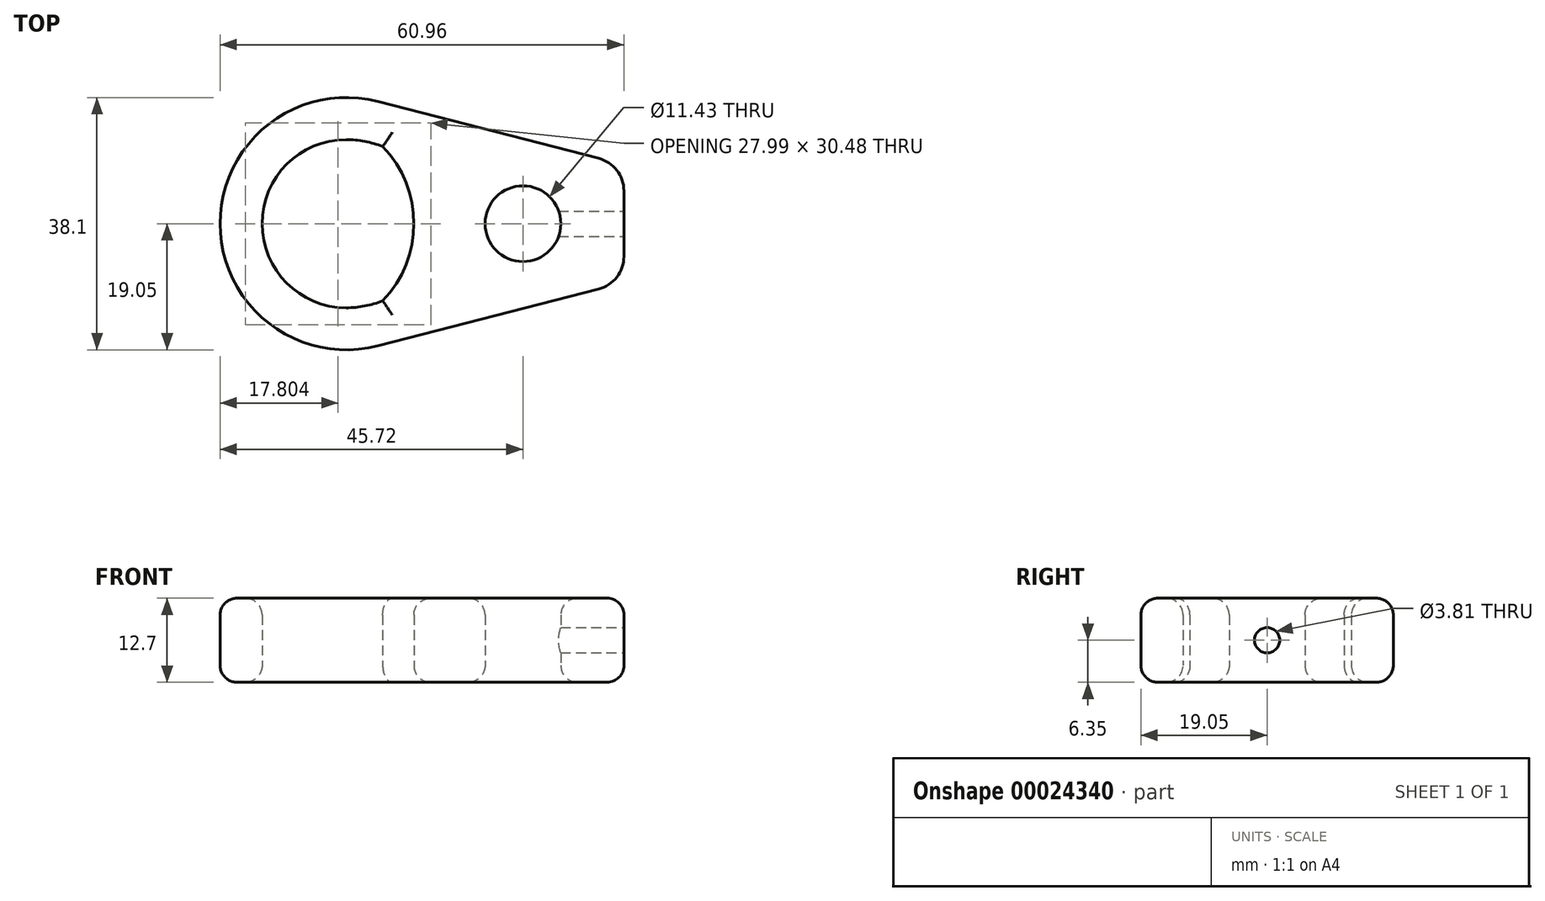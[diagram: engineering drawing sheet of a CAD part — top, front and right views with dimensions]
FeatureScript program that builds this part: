
annotation { "Feature Type Name" : "Feature", "Feature Type Description" : "" }
export const myFeature = defineFeature(function(context is Context, id is Id, definition is map)
    precondition{}
    {
        {
            var Q0;
            Q0=qCreatedBy(makeId("Top.planeOp"),FACE);
            var sketch = newSketch(context, id + "F0", { "sketchPlane" : qUnion([Q0])});
            skLineSegment(sketch, "E0", {"start": v(41.9, -8.89) * mm, "end": v(4.75, -18.45) * mm});
            skLineSegment(sketch, "E1", {"start": v(41.9, 8.89) * mm, "end": v(4.75, 18.45) * mm});
            skArc(sketch, "E2", {"start": v(4.75, -18.45) * mm, "mid": v(-19.05, 0) * mm, "end": v(4.75, 18.45) * mm});
            skLineSegment(sketch, "E3", {"start": v(41.91, -8.89) * mm, "end": v(41.9, 8.89) * mm});
            skLineSegment(sketch, "E4", {"start": v(-103.71, 0) * mm, "end": v(103.01, 0) * mm, "construction": true});
            skPoint(sketch, "E5", {"position": v(41.91, 0) * mm});
            skLineSegment(sketch, "E6", {"start": v(4.75, -62.77) * mm, "end": v(4.75, 84.05) * mm, "construction": true});
            skArc(sketch, "E7", {"start": v(0, 12.7) * mm, "mid": v(-12.7, 0) * mm, "end": v(0, -12.7) * mm});
            skArc(sketch, "E8", {"start": v(5.5, -11.65) * mm, "mid": v(10.2, 0) * mm, "end": v(5.5, 11.65) * mm});
            skArc(sketch, "E9", {"start": v(0, -12.7) * mm, "mid": v(2.8, -12.43) * mm, "end": v(5.5, -11.65) * mm});
            skArc(sketch, "E10", {"start": v(0, 12.7) * mm, "mid": v(2.8, 12.43) * mm, "end": v(5.5, 11.65) * mm});
            skLineSegment(sketch, "E11", {"start": v(5.5, -62.77) * mm, "end": v(5.5, 84.05) * mm, "construction": true});
            skCircle(sketch, "E12", {"center": v(26.67, 0) * mm, "radius": 5.72 * mm});
            skSolve(sketch);
        }
        {
            var Q0;
            Q0=makeQuery(id+"F0.imprint","IMPRINT",FACE,{"disambiguationData":[TD([[makeQuery(id+"F0.imprint","IMPRINT",EDGE,{"derivedFrom":sQuery(id+"F0.wireOp",EDGE,"E0")}),-1.0]])]});
            extrude(context, id + "F1", {"entities" : qUnion([Q0]), "depth" : 12.7 * mm});
        }
        {
            var Q0;
            Q0=makeQuery(id+"F1.opExtrude","SWEPT_EDGE",EDGE,{"disambiguationData":[OSD([sQuery(id+"F0.wireOp",EDGE,"E0"),sQuery(id+"F0.wireOp",EDGE,"E3")])]});
            var Q1;
            Q1=makeQuery(id+"F1.opExtrude","SWEPT_EDGE",EDGE,{"disambiguationData":[OSD([sQuery(id+"F0.wireOp",EDGE,"E1"),sQuery(id+"F0.wireOp",EDGE,"E3")])]});
            fillet(context, id + "F2", {"entities" : qUnion([Q0, Q1]), "radius" : 5.08 * mm, "tangentPropagation" : true, "allowEdgeOverflow" : false});
        }
        {
            var Q0;
            Q0=makeQuery(id+"F1.opExtrude","CAP_FACE",FACE,{"disambiguationData":[OSD([sQuery(id+"F0.wireOp",EDGE,"E0"),sQuery(id+"F0.wireOp",EDGE,"E1"),sQuery(id+"F0.wireOp",EDGE,"E2"),sQuery(id+"F0.wireOp",EDGE,"E3"),sQuery(id+"F0.wireOp",EDGE,"E7"),sQuery(id+"F0.wireOp",EDGE,"E8"),sQuery(id+"F0.wireOp",EDGE,"E9"),sQuery(id+"F0.wireOp",EDGE,"E10"),sQuery(id+"F0.wireOp",EDGE,"E12")])],"isStart":false});
            var Q1;
            Q1=makeQuery(id+"F1.opExtrude","CAP_FACE",FACE,{"disambiguationData":[OSD([sQuery(id+"F0.wireOp",EDGE,"E0"),sQuery(id+"F0.wireOp",EDGE,"E1"),sQuery(id+"F0.wireOp",EDGE,"E2"),sQuery(id+"F0.wireOp",EDGE,"E3"),sQuery(id+"F0.wireOp",EDGE,"E7"),sQuery(id+"F0.wireOp",EDGE,"E8"),sQuery(id+"F0.wireOp",EDGE,"E9"),sQuery(id+"F0.wireOp",EDGE,"E10"),sQuery(id+"F0.wireOp",EDGE,"E12")])],"isStart":true});
            fillet(context, id + "F3", {"entities" : qUnion([Q0, Q1]), "radius" : 2.54 * mm, "tangentPropagation" : true, "allowEdgeOverflow" : false});
        }
        {
            var Q0;
            Q0=makeQuery(id+"F1.opExtrude","SWEPT_FACE",FACE,{"disambiguationData":[OSD([sQuery(id+"F0.wireOp",EDGE,"E3")])]});
            var sketch = newSketch(context, id + "F4", { "sketchPlane" : qUnion([Q0])});
            skLineSegment(sketch, "E13.0", {"start": v(-4.95, 10.16) * mm, "end": v(-4.95, 2.54) * mm, "construction": true});
            skLineSegment(sketch, "E14.0", {"start": v(4.95, 2.54) * mm, "end": v(4.95, 10.16) * mm, "construction": true});
            skLineSegment(sketch, "E15", {"start": v(-4.95, 6.35) * mm, "end": v(4.95, 6.35) * mm, "construction": true});
            skPoint(sketch, "E16", {"position": v(0, 6.35) * mm});
            skSolve(sketch);
        }
        {
            var Q0;
            Q0=sQuery(id+"F4.wireOp",VERTEX,"E16");
            var Q1;
            Q1=makeQuery(id+"F1.opExtrude","SWEPT_BODY",BODY,{"disambiguationData":[OSD([sQuery(id+"F0.wireOp",EDGE,"E0"),sQuery(id+"F0.wireOp",EDGE,"E1"),sQuery(id+"F0.wireOp",EDGE,"E2"),sQuery(id+"F0.wireOp",EDGE,"E3"),sQuery(id+"F0.wireOp",EDGE,"E7"),sQuery(id+"F0.wireOp",EDGE,"E8"),sQuery(id+"F0.wireOp",EDGE,"E9"),sQuery(id+"F0.wireOp",EDGE,"E10"),sQuery(id+"F0.wireOp",EDGE,"E12")])]});
            hole(context, id + "F5", {"style" : HoleStyle.SIMPLE, "holeDiameter" : 3.8 * mm, "endStyle" : HoleEndStyle.BLIND, "holeDepth" : 12.7 * mm, "locations" : qUnion([Q0]), "scope" : qUnion([Q1])});
        }
    });
